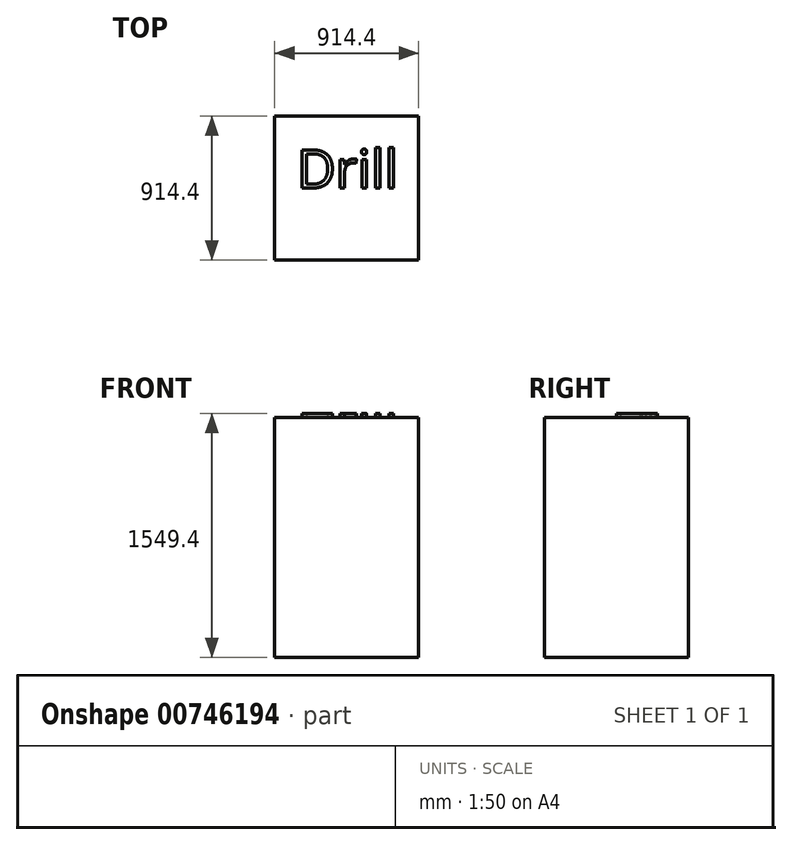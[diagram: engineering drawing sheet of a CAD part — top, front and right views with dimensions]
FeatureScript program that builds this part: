
annotation { "Feature Type Name" : "Feature", "Feature Type Description" : "" }
export const myFeature = defineFeature(function(context is Context, id is Id, definition is map)
    precondition{}
    {
        {
            var Q0;
            Q0=qCreatedBy(makeId("Top.planeOp"),FACE);
            var sketch = newSketch(context, id + "F0", { "sketchPlane" : qUnion([Q0])});
            skLineSegment(sketch, "E0.bottom", {"start": v(457.2, -457.2) * mm, "end": v(-457.2, -457.2) * mm});
            skLineSegment(sketch, "E0.top", {"start": v(457.2, 457.2) * mm, "end": v(-457.2, 457.2) * mm});
            skLineSegment(sketch, "E0.left", {"start": v(457.2, -457.2) * mm, "end": v(457.2, 457.2) * mm});
            skLineSegment(sketch, "E0.right", {"start": v(-457.2, -457.2) * mm, "end": v(-457.2, 457.2) * mm});
            skPoint(sketch, "E0.middle", {"position": v(0, 0) * mm});
            skSolve(sketch);
        }
        {
            var Q0;
            Q0 = qSketchRegion(id + "F0", true);
            extrude(context, id + "F1", {"entities" : qUnion([Q0]), "depth" : 1524 * mm, "offsetDistance" : 25.4 * mm});
        }
        {
            var Q0;
            Q0=makeQuery(id+"F1.opExtrude","CAP_FACE",FACE,{"disambiguationData":[OSD([sQuery(id+"F0.wireOp",EDGE,"E0.bottom"),sQuery(id+"F0.wireOp",EDGE,"E0.top"),sQuery(id+"F0.wireOp",EDGE,"E0.left"),sQuery(id+"F0.wireOp",EDGE,"E0.right")])],"isStart":false});
            var sketch = newSketch(context, id + "F2", { "sketchPlane" : qUnion([Q0])});
            skText(sketch, "E1", { "text": "Drill", "fontName": "OpenSans-Regular.ttf"});
            const initialGuessF2  = {"E1": [-0.3175, 0, 1, 0, 0.24382]};
            skSetInitialGuess(sketch, initialGuessF2);
            skSolve(sketch);
        }
        {
            var Q0;
            Q0 = qSketchRegion(id + "F2", true);
            extrude(context, id + "F3", {"entities" : qUnion([Q0]), "operationType" : NewBodyOperationType.ADD, "depth" : 25.4 * mm, "offsetDistance" : 25.4 * mm});
        }
    });
